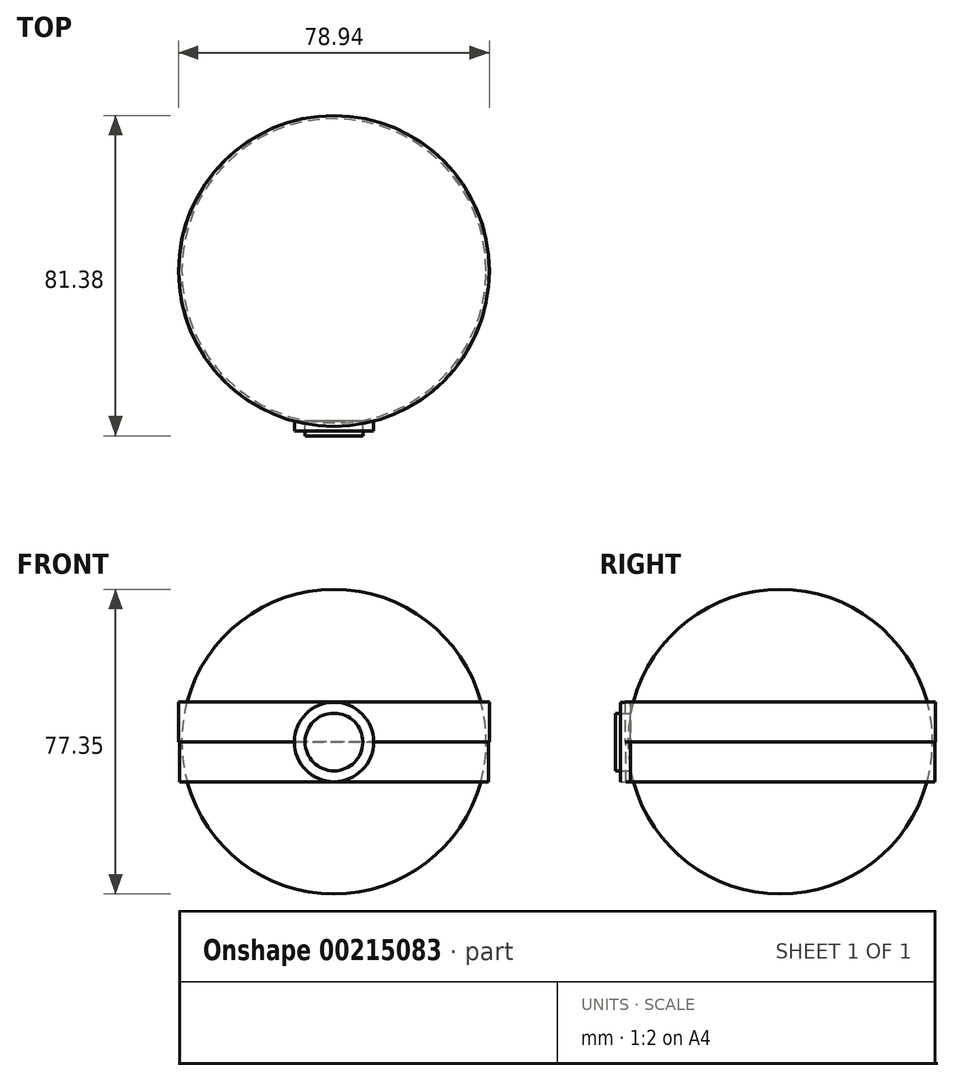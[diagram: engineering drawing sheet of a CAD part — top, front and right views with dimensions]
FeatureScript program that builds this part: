
annotation { "Feature Type Name" : "Feature", "Feature Type Description" : "" }
export const myFeature = defineFeature(function(context is Context, id is Id, definition is map)
    precondition{}
    {
        {
            var Q0;
            Q0=qCreatedBy(makeId("Front.planeOp"),FACE);
            var sketch = newSketch(context, id + "F0", { "sketchPlane" : qUnion([Q0])});
            skArc(sketch, "E0", {"start": v(0, -38.58) * mm, "mid": v(38.68, 0.1) * mm, "end": v(0, 38.77) * mm});
            skLineSegment(sketch, "E1", {"start": v(0, 38.77) * mm, "end": v(0, -38.58) * mm});
            skSolve(sketch);
        }
        {
            var Q0;
            Q0=makeQuery(id+"F0.imprint","IMPRINT",FACE,{"disambiguationData":[TD([[makeQuery(id+"F0.imprint","IMPRINT",EDGE,{"derivedFrom":sQuery(id+"F0.wireOp",EDGE,"E0")}),1.0]])]});
            var Q1;
            Q1=sQuery(id+"F0.wireOp",EDGE,"E1");
            revolve(context, id + "F1", {"entities" : qUnion([Q0]), "axis" : qUnion([Q1]), "revolveType" : RevolveType.FULL});
        }
        {
            var Q0;
            Q0=qCreatedBy(makeId("Front.planeOp"),FACE);
            cPlane(context, id + "F2", {"entities" : qUnion([Q0]), "cplaneType" : CPlaneType.OFFSET, "offset" : 38.1 * mm, "width" : 152.4 * mm, "height" : 152.4 * mm});
        }
        {
            var Q0;
            Q0=qCreatedBy(id+"F2.planeOp",FACE);
            var sketch = newSketch(context, id + "F3", { "sketchPlane" : qUnion([Q0])});
            skCircle(sketch, "E2", {"center": v(0, 0) * mm, "radius": 7.32 * mm});
            skSolve(sketch);
        }
        {
            var Q0;
            Q0 = qSketchRegion(id + "F3", true);
            extrude(context, id + "F4", {"entities" : qUnion([Q0]), "depth" : 3.8 * mm});
        }
        {
            var Q0;
            Q0=qCreatedBy(id+"F2.planeOp",FACE);
            var sketch = newSketch(context, id + "F5", { "sketchPlane" : qUnion([Q0])});
            skCircle(sketch, "E3", {"center": v(0, 0) * mm, "radius": 10.08 * mm});
            skSolve(sketch);
        }
        {
            var Q0;
            Q0 = qSketchRegion(id + "F5", true);
            extrude(context, id + "F6", {"entities" : qUnion([Q0]), "depth" : 2.54 * mm});
        }
        {
            var Q0;
            Q0=qCreatedBy(makeId("Top.planeOp"),FACE);
            var sketch = newSketch(context, id + "F7", { "sketchPlane" : qUnion([Q0])});
            skCircle(sketch, "E4", {"center": v(0, 0) * mm, "radius": 39.47 * mm});
            skSolve(sketch);
        }
        {
            var Q0;
            Q0 = qSketchRegion(id + "F7", true);
            extrude(context, id + "F8", {"entities" : qUnion([Q0]), "depth" : 10.16 * mm});
        }
        {
            var Q0;
            Q0=qCreatedBy(makeId("Top.planeOp"),FACE);
            var sketch = newSketch(context, id + "F9", { "sketchPlane" : qUnion([Q0])});
            skCircle(sketch, "E5", {"center": v(0, 0) * mm, "radius": 39.23 * mm});
            skSolve(sketch);
        }
        {
            var Q0;
            Q0 = qSketchRegion(id + "F9", true);
            extrude(context, id + "F10", {"entities" : qUnion([Q0]), "oppositeDirection" : true, "depth" : 10.16 * mm});
        }
    });
